# Revit family: RSen_55_ME_FB_outdoor unit - altherma_daikin
name_source: partatom
category: Mechanical Equipment
units: mm (PartAtom-declared; Revit-internal decimal feet)

## family parameters
Cut with Voids When Loaded = No
Host = Face
OmniClass Number = 23.75.10.21.14
OmniClass Title = Rooftop Heat Pumps
Part Type = Normal
Room Calculation Point = No
Round Connector Dimension = Use Diameter
Shared = No

## types (1)
- TYPE CATALOG
    Assembly Code = 56.10.10
    COP = 4.30 (1)/2.65 (3)/3.32 (2)/2.08 (4)
    Casing Colour = Ivory white
    Current Recommended fuses A = 40 A
    Default Elevation = 0 mm  [stored 0 ft]
    Description = Heating Only
    Dimensions Unit Height/Width/Depth mm = 1348/1160/380 mm
    Heating capacity Max. kW = 10.60 (3)/10.80 (4) kW
    Heating capacity Nom. kW = 14.5 (1)/13.6 (2) kW
    IfcExportAs = IfcUnitaryEquipmentType
    IfcExportType = AIRCONDITIONINGUNIT
    Installation Manual = http://www.daikineurope.com
    Manufacturer = Daikin Europe N.V.
    Model = Altherma
    Operation range Cooling Ambient Min./Max. °CDB = -
    Operation range Cooling Water side Min./Max. °C = -
    Operation range Domestic hot water Ambient Min./Max. °CDB = -25 °CDB/35 °CDB
    Operation range Domestic hot water Water side Min./Max. °C = 25 °C/80 °C
    Operation range Heating Ambient Min./Max. °CWB = -10 °CWB/35 °CWB
    Operation range Heating Water side Min./Max. °C = -15 °C/55 °C
    Piping connections High and low pressure gas OD mm = -
    Piping connections Liquid OD mm = -
    Piping connections Suction OD mm = -
    Power input Heating Nom. kW = 3.37 (1)/4.10 (2) kW
    Power supply Phase/Frequency Hz/Voltage V = 1~/50 Hz/230 V
    RSen_C_IFC_version = 2x3
    RSen_C_code_article = EDLQ014CAV3
    RSen_C_code_product = EDLQ014CV3
    RSen_C_code_product_class = EDLQ
    RSen_C_content_date_changed = 31/07/2018
    RSen_C_content_date_issue = 31/07/2018
    RSen_C_content_provider = Daikin Europe N.V.
    RSen_C_content_version = 1.1.0
    RSen_C_description = Heating Only
    RSen_C_diameter_type = OD
    RSen_C_diameter_type_index = 1
    RSen_C_license = Creative Commons Attribution NoDerivs (CC-ND)
    RSen_C_license_info = https://tldrlegal.com
    RSen_C_material = RSen_x_rgb 202 196 176 T00 silk gray_gen
    RSen_C_model = Altherma
    RSen_C_revit_version = 2016
    RSen_C_type = Heating
    RSen_C_type_comments = Outdoor unit
    RSen_E_c01_apparent_power = 0 VA
    RSen_E_c01_apparent_power_phase_1 = 0 VA
    RSen_E_c01_apparent_power_phase_2 = 0 VA
    RSen_E_c01_apparent_power_phase_3 = 0 VA
    RSen_E_c01_current = 0 A
    RSen_E_c01_description = c01_el
    RSen_E_c01_division_engine = No
    RSen_E_c01_load_class = Other
    RSen_E_c01_number_of_poles = 1
    RSen_E_c01_power = 0 W
    RSen_E_c01_power_factor = 1
    RSen_E_c01_power_factor_state = Lagging
    RSen_E_c01_system_type = Power - Unbalanced
    RSen_E_c01_voltage = 230 V
    RSen_E_c01_yes_no = Yes
    RSen_E_c02_description = c02_controls
    RSen_E_c02_yes_no = Yes
    RSen_P_c01_description = c01_water out connection
    RSen_P_c01_diameter = 25 mm  [stored 0.082021 ft]
    RSen_P_c01_diameter_calc = 25 mm  [stored 0.082021 ft]
    RSen_P_c01_flow_configuration = Calculated
    RSen_P_c01_flow_direction = Out
    RSen_P_c01_loss_method = Not Defined
    RSen_P_c01_system_classification = Hydronic Supply
    RSen_P_c01_yes_no = Yes
    RSen_P_c02_description = c02_water in conection
    RSen_P_c02_diameter = 25 mm  [stored 0.082021 ft]
    RSen_P_c02_diameter_calc = 25 mm  [stored 0.082021 ft]
    RSen_P_c02_flow_configuration = Calculated
    RSen_P_c02_flow_direction = In
    RSen_P_c02_loss_method = Not Defined
    RSen_P_c02_system_classification = Hydronic Return
    RSen_P_c02_yes_no = Yes
    Refrigerant Charge kg = 3.40 kg
    Refrigerant Type = R-410A
    Sound power level Cooling Nom. dBA = 66 dBA
    Sound power level Heating Nom. dBA = 64 dBA
    Sound pressure level Cooling Nom. dBA = 52 dBA
    Sound pressure level Heating Nom. dBA = 51 dBA
    Sound pressure level Night quiet mode Cooling dBA = 45 dBA
    Sound pressure level Night quiet mode Heating dBA = 42 dBA
    Specification Text = https://my.daikin.eu
    TBQ_I BaseKeynote = 56.10.10
    TBQ_I Spacing_default = 0 mm  [stored 0 ft]
    TBQ_I Spacing_minimum = 0 mm  [stored 0 ft]
    TBQen_C_SOg_01 = GEO_none_daikin : standard
    TBQen_C_SOg_02 = GEO_none_daikin : standard
    TBQen_C_SOg_03 = GEO_none_daikin : standard
    TBQen_C_SOg_04 = GEO_none_daikin : standard
    Type Comments = Outdoor unit
    URL = www.daikineurope.com
    Water circuit Piping connections diameter inch = G 1"1/4 (female) inch
    Weight Unit kg = 151 kg
    ZZZ_Component_01_Y_Length = 0 mm  [stored 0 ft]
    ZZZ_Component_01_Z_Length = 0 mm  [stored 0 ft]
    ZZZ_Component_02_Y_Length = 0 mm  [stored 0 ft]
    ZZZ_Component_02_Z_Length = 0 mm  [stored 0 ft]
    ZZZ_Component_03_Y_Length = 0 mm  [stored 0 ft]
    ZZZ_Component_03_Z_Length = 0 mm  [stored 0 ft]
    ZZZ_Component_04_Y_Length = 0 mm  [stored 0 ft]
    ZZZ_Component_04_Z_Length = 0 mm  [stored 0 ft]
    ZZZ_Housing_medium and coarse_FamilyType_Mechanical Equipment = GEO_medium and coarse_daikin : standard
    ZZZ_Logo_Z_Length = -29 mm  [stored -0.0951444 ft]
    ZZZ_Logo_left side_YesNo = No
    ZZZ_Logo_plane_Integer = 3
    ZZZ_Logo_right side_YesNo = Yes
    ZZZ_Lookup table name_Text = RSen_55_ME_FB_indoor unit - outdoor unit
    ZZZ_Offset_Length = 1000 mm  [stored 3.28084 ft]
    ZZZ_V Clearance behind unit_Length = 600 mm  [stored 1.9685 ft]
    ZZZ_V Clearance zone_back_Length = 0 mm  [stored 0 ft]
    ZZZ_V Clearance zone_bottom_Length = 0 mm  [stored 0 ft]
    ZZZ_V Clearance zone_front_Length = 0 mm  [stored 0 ft]
    ZZZ_V Clearance zone_left_Length = 0 mm  [stored 0 ft]
    ZZZ_V Clearance zone_material_Material = RSen_x_rgb 255 128 128 T80 red_gen
    ZZZ_V Clearance zone_right_Length = 0 mm  [stored 0 ft]
    ZZZ_V Clearance zone_top_Length = 0 mm  [stored 0 ft]
    ZZZ_V Component_01_description_Text = EDLQ014CAV3
    ZZZ_V Component_01_fan_X_Length = -272 mm
    ZZZ_V Component_01_fan_Y_Length = 2 mm  [stored 0.00656168 ft]
    ZZZ_V Component_01_fan_Z_Length = 0 mm  [stored 0 ft]
    ZZZ_V Component_01_fan_height_Length = 29 mm  [stored 0.0951444 ft]
    ZZZ_V Component_01_fan_length_Length = 540 mm  [stored 1.77165 ft]
    ZZZ_V Component_01_fan_material_Material = RSen_x_rgb 189 187 185 T80 gray_gen
    ZZZ_V Component_01_fan_plane_Integer = 3
    ZZZ_V Component_01_fan_width_Length = 1100 mm
    ZZZ_V Component_01_height_Length = 1348 mm  [stored 4.42257 ft]
    ZZZ_V Component_01_length_Length = 1156 mm  [stored 3.79265 ft]
    ZZZ_V Component_01_material_Material = RSen_x_rgb 202 196 176 T00 silk gray_gen
    ZZZ_V Component_01_width_Length = 351 mm  [stored 1.15157 ft]
    ZZZ_V Component_02_description_Text = -
    ZZZ_V Component_02_fan_X_Length = 0 mm  [stored 0 ft]
    ZZZ_V Component_02_fan_Y_Length = 0 mm  [stored 0 ft]
    ZZZ_V Component_02_fan_Z_Length = 0 mm  [stored 0 ft]
    ZZZ_V Component_02_fan_height_Length = 0 mm  [stored 0 ft]
    ZZZ_V Component_02_fan_length_Length = 0 mm  [stored 0 ft]
    ZZZ_V Component_02_fan_material_Material = <By Category>
    ZZZ_V Component_02_fan_plane_Integer = 1
    ZZZ_V Component_02_fan_width_Length = 0 mm  [stored 0 ft]
    ZZZ_V Component_02_height_Length = 0 mm  [stored 0 ft]
    ZZZ_V Component_02_length_Length = 0 mm  [stored 0 ft]
    ZZZ_V Component_02_material_Material = <By Category>
    ZZZ_V Component_02_width_Length = 0 mm  [stored 0 ft]
    ZZZ_V Component_03_description_Text = -
    ZZZ_V Component_03_fan_X_Length = 0 mm  [stored 0 ft]
    ZZZ_V Component_03_fan_Y_Length = 0 mm  [stored 0 ft]
    ZZZ_V Component_03_fan_Z_Length = 0 mm  [stored 0 ft]
    ZZZ_V Component_03_fan_height_Length = 0 mm  [stored 0 ft]
    ZZZ_V Component_03_fan_length_Length = 0 mm  [stored 0 ft]
    ZZZ_V Component_03_fan_material_Material = <By Category>
    ZZZ_V Component_03_fan_plane_Integer = 1
    ZZZ_V Component_03_fan_width_Length = 0 mm  [stored 0 ft]
    ZZZ_V Component_03_height_Length = 0 mm  [stored 0 ft]
    ZZZ_V Component_03_length_Length = 0 mm  [stored 0 ft]
    ZZZ_V Component_03_material_Material = <By Category>
    ZZZ_V Component_03_width_Length = 0 mm  [stored 0 ft]
    ZZZ_V Component_04_description_Text = -
    ZZZ_V Component_04_fan_X_Length = 0 mm  [stored 0 ft]
    ZZZ_V Component_04_fan_Y_Length = 0 mm  [stored 0 ft]
    ZZZ_V Component_04_fan_Z_Length = 0 mm  [stored 0 ft]
    ZZZ_V Component_04_fan_height_Length = 0 mm  [stored 0 ft]
    ZZZ_V Component_04_fan_length_Length = 0 mm  [stored 0 ft]
    ZZZ_V Component_04_fan_material_Material = <By Category>
    ZZZ_V Component_04_fan_plane_Integer = 1
    ZZZ_V Component_04_fan_width_Length = 0 mm  [stored 0 ft]
    ZZZ_V Component_04_height_Length = 0 mm  [stored 0 ft]
    ZZZ_V Component_04_length_Length = 0 mm  [stored 0 ft]
    ZZZ_V Component_04_material_Material = <By Category>
    ZZZ_V Component_04_width_Length = 0 mm  [stored 0 ft]
    ZZZ_V Connection zone_back_Length = 0 mm  [stored 0 ft]
    ZZZ_V Connection zone_bottom_Length = 0 mm  [stored 0 ft]
    ZZZ_V Connection zone_front_Length = 0 mm  [stored 0 ft]
    ZZZ_V Connection zone_left_Length = 0 mm  [stored 0 ft]
    ZZZ_V Connection zone_material_Material = RSen_x_rgb 255 128 128 T80 red_gen
    ZZZ_V Connection zone_right_Length = 0 mm  [stored 0 ft]
    ZZZ_V Connection zone_top_Length = 0 mm  [stored 0 ft]
    ZZZ_V E_c01_X_Length = 0 mm  [stored 0 ft]
    ZZZ_V E_c01_Y_Length = 0 mm  [stored 0 ft]
    ZZZ_V E_c01_Z_Length = -300 mm  [stored -0.984252 ft]
    ZZZ_V E_c01_plane_Integer = 2
    ZZZ_V Logo_FamilyType_Generic Models = RSen_55_GM_FB_logo outdoor unit - SH_daikin : standard
    ZZZ_V Maintenance zone_back_Length = 0 mm  [stored 0 ft]
    ZZZ_V Maintenance zone_bottom_Length = 0 mm  [stored 0 ft]
    ZZZ_V Maintenance zone_front_Length = 0 mm  [stored 0 ft]
    ZZZ_V Maintenance zone_left_Length = 0 mm  [stored 0 ft]
    ZZZ_V Maintenance zone_material_Material = RSen_x_rgb 255 128 128 T80 red_gen
    ZZZ_V Maintenance zone_right_Length = 0 mm  [stored 0 ft]
    ZZZ_V Maintenance zone_top_Length = 0 mm  [stored 0 ft]
    ZZZ_V Neighbour unit_offset_back_Length = 0 mm  [stored 0 ft]
    ZZZ_V Neighbour unit_offset_front_Length = 0 mm  [stored 0 ft]
    ZZZ_V Neighbour unit_offset_left_Length = 0 mm  [stored 0 ft]
    ZZZ_V Neighbour unit_offset_right_Length = 0 mm  [stored 0 ft]
    ZZZ_V P_c01_X_Length = -411 mm  [stored -1.34843 ft]
    ZZZ_V P_c01_Y_Length = -618 mm  [stored -2.02756 ft]
    ZZZ_V P_c01_Z_Length = 32 mm  [stored 0.104987 ft]
    ZZZ_V P_c01_length_Length = 32 mm  [stored 0.104987 ft]
    ZZZ_V P_c01_plane_Integer = 4
    ZZZ_V P_c02_X_Length = -512 mm  [stored -1.67979 ft]
    ZZZ_V P_c02_Y_Length = -558 mm
    ZZZ_V P_c02_Z_Length = 32 mm  [stored 0.104987 ft]
    ZZZ_V P_c02_length_Length = 32 mm  [stored 0.104987 ft]
    ZZZ_V P_c02_plane_Integer = 4
    ZZZ_V Placement zone_material_Material = RSen_x_rgb 255 128 128 T80 red_gen
    ZZZ_Visualized connectors_FamilyType_Generic Models = RSen_55_GM_FB_none_daikin : standard
    ZZZ_Zones_plane_Integer = 2

note: [stored X ft] marks values corroborated as IEEE doubles in the binary element streams (Revit-internal decimal feet)

## geometry (parser evidence)
native form markers: Sweep x42
no freeform markers — native parametric forms only
